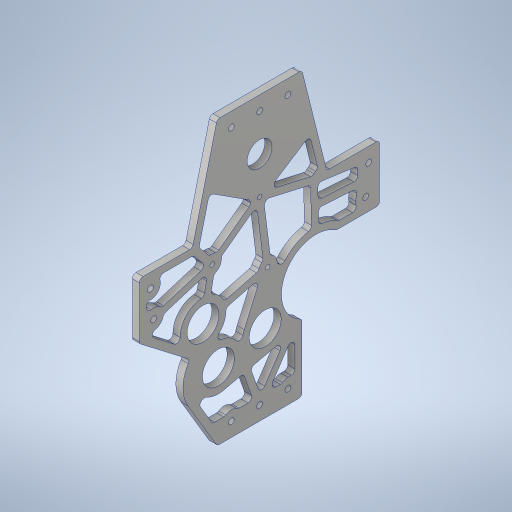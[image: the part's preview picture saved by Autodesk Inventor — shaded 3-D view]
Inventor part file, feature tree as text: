
AUTODESK INVENTOR PART (.ipt)
format: ipt  version: 2023.4 (Build 274418000, 418)  size: 838,656 bytes
history: native  units: in
note: dims shown in document units (in); Inventor stores cm internally (conversion verified against a paired STEP export)
features: sketch x6, hole x4, projected_geometry x3, extrude x2, fillet x2
ambient origin geometry x8: Origin, YZ Plane, XZ Plane, XY Plane, X Axis, Y Axis, Z Axis, Center Point
bodies: Solid1 (feature_tree)
feature tree (17):
  sketch  "Sketch1"  dims[d0=10.0in d1=1.0in]
  sketch  "Sketch2"  dims[d2=3.25in d3=1.0in]
  extrude  "Extrusion1"  Depth=10.0in
  hole  "Mount Holes"  [1 undecoded]
  hole  "Hole4"  [1 undecoded]
  hole  "Hole5"  [1 undecoded]
  hole  "Hole6"  [1 undecoded]
  extrude  "Extrusion5"  Depth=0.13in
  fillet  "Fillet5"  Radius=2.5in
  fillet  "Fillet6"  Radius=1.2in
  sketch  "Sketch7"  dims[d4=1.942in d6=3.5in]
  sketch  "Sketch8"  dims[d7=0.123in d8=1.0in]
  sketch  "Sketch9"  dims[d9=1.0in d10=0.6in]
  sketch  "Sketch10"  dims[d11=3.3in d12=0.9in d13=2.5in d14=1.2in d15=2.2in d16=2.45in d19=2.5in d23=0.8in d24=1.125in d26=1.0in d27=1.0in d28=1.0in d29=1.0in d30=0.25in d31=0.25in d32=0.25in d33=1.375in d34=2.0in d35=2.3622in d37=360.0deg d41=0.125in d42=3.0in d44=0.25in d45=0.0in d46=0.201in d47=0.75in d48=0.385in d49=0.25in d50=0.5635in d51=1.0in d52=0.8108in d60=4.006in d63=1.25in d64=1.75in d66=1.375in d67=1.25in d68=0.875in d70=0.375in d71=1.875in d73=4.6532in d74=0.5in d75=1.432in d76=4.297in d78=0.391in d79=0.391in d137=0.5in d149=8.0944in d151=1.8013in d152=4.4272in d153=0.25in d154=4.297in d155=1.432in d175=0.156in d176=0.38in d177=0.375in d178=0.25in d179=0.5635in d180=1.0in d181=0.8108in d183=2.624in d184=0.156in d185=0.38in d186=0.375in d187=0.25in d188=0.5635in d189=1.0in d190=0.8108in d194=1.625in d197=0.375in d198=0.375in d199=1.125in d201=1.432in d202=4.297in d204=2.0in d205=4.2014in d206=1.074in d207=2.2385in d208=75.0deg d209=0.156in d210=0.38in d211=0.385in d212=0.25in d213=0.5635in d214=1.0in d215=0.8108in d216=0.25in d218=0.25in d219=0.25in d220=0.25in d221=0.25in d222=0.25in d223=0.25in d224=0.25in d225=0.25in d226=0.25in d227=0.25in d228=0.25in d229=0.25in d230=0.25in d231=0.125in d232=0.125in d233=0.125in d234=0.125in d235=0.125in d236=0.125in d237=0.125in d238=0.125in d239=0.25in d240=0.25in d241=0.125in d242=0.125in d243=0.25in d244=1.0in d245=0.0in d246=0.125in d247=0.125in d248=0.125in d249=0.25in d250=0.125in d251=0.125in d252=0.125in d253=0.125in d254=0.125in d256=0.125in d257=0.656in d258=0.656in d259=0.125in d260=0.125in d261=0.13in d262=0.13in]
  projected_geometry  "Project Cut Edges4"
  projected_geometry  "Project Cut Edges5"
  projected_geometry  "Project Cut Edges6"
note: 4 required parameter values undecoded (feature->parameter linkage not recoverable at this tier; creation-order binding heuristic only, values carry confidence <= 0.55)
